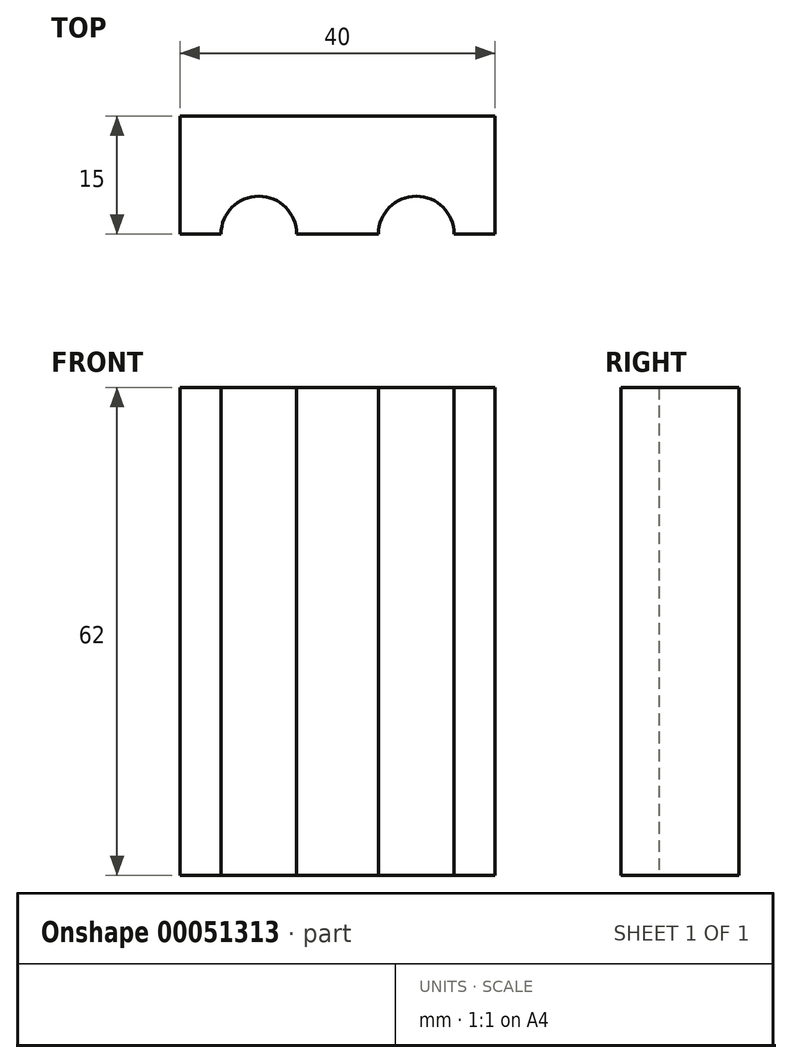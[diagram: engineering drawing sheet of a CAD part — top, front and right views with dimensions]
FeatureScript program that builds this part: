
annotation { "Feature Type Name" : "Feature", "Feature Type Description" : "" }
export const myFeature = defineFeature(function(context is Context, id is Id, definition is map)
    precondition{}
    {
        {
            var Q0;
            Q0=qCreatedBy(makeId("Top.planeOp"),FACE);
            var sketch = newSketch(context, id + "F0", { "sketchPlane" : qUnion([Q0])});
            skLineSegment(sketch, "E0.bottom", {"start": v(0, 0) * mm, "end": v(40, 0) * mm});
            skLineSegment(sketch, "E0.top", {"start": v(0, 15) * mm, "end": v(40, 15) * mm});
            skLineSegment(sketch, "E0.left", {"start": v(0, 0) * mm, "end": v(0, 15) * mm});
            skLineSegment(sketch, "E0.right", {"start": v(40, 0) * mm, "end": v(40, 15) * mm});
            skSolve(sketch);
        }
        {
            var Q0;
            Q0=makeQuery(id+"F0.imprint","IMPRINT",FACE,{"disambiguationData":[TD([[makeQuery(id+"F0.imprint","IMPRINT",EDGE,{"derivedFrom":sQuery(id+"F0.wireOp",EDGE,"E0.bottom")}),1.0]])]});
            extrude(context, id + "F1", {"entities" : qUnion([Q0]), "depth" : 62 * mm});
        }
        {
            var Q0;
            Q0=makeQuery(id+"F1.opExtrude","CAP_FACE",FACE,{"disambiguationData":[OSD([sQuery(id+"F0.wireOp",EDGE,"E0.bottom"),sQuery(id+"F0.wireOp",EDGE,"E0.top"),sQuery(id+"F0.wireOp",EDGE,"E0.left"),sQuery(id+"F0.wireOp",EDGE,"E0.right")])],"isStart":true});
            var sketch = newSketch(context, id + "F2", { "sketchPlane" : qUnion([Q0])});
            skLineSegment(sketch, "E1", {"start": v(20, 0) * mm, "end": v(20, -15) * mm, "construction": true});
            skLineSegment(sketch, "E2", {"start": v(10, 0) * mm, "end": v(10, -15) * mm, "construction": true});
            skLineSegment(sketch, "E3", {"start": v(30, 0) * mm, "end": v(30, -15) * mm, "construction": true});
            skArc(sketch, "E4", {"start": v(5.2, 0) * mm, "mid": v(10, -4.8) * mm, "end": v(14.8, 0) * mm});
            skArc(sketch, "E5", {"start": v(25.2, 0) * mm, "mid": v(30, -4.8) * mm, "end": v(34.8, 0) * mm});
            skSolve(sketch);
        }
        {
            var Q0;
            {var subQ0=sQuery(id+"F2.wireOp",EDGE,"E4");Q0=makeQuery(id+"F2.imprint","IMPRINT",FACE,{"disambiguationData":[TD([[makeQuery(id+"F2.imprint","IMPRINT",EDGE,{"derivedFrom":subQ0}),1.0]])]});}
            var Q1;
            {var subQ0=sQuery(id+"F2.wireOp",EDGE,"E5");Q1=makeQuery(id+"F2.imprint","IMPRINT",FACE,{"disambiguationData":[TD([[makeQuery(id+"F2.imprint","IMPRINT",EDGE,{"derivedFrom":subQ0}),1.0]])]});}
            extrude(context, id + "F3", {"entities" : qUnion([Q0, Q1]), "operationType" : NewBodyOperationType.REMOVE, "endBound" : BoundingType.THROUGH_ALL, "oppositeDirection" : true, "depth" : 25 * mm});
        }
    });
